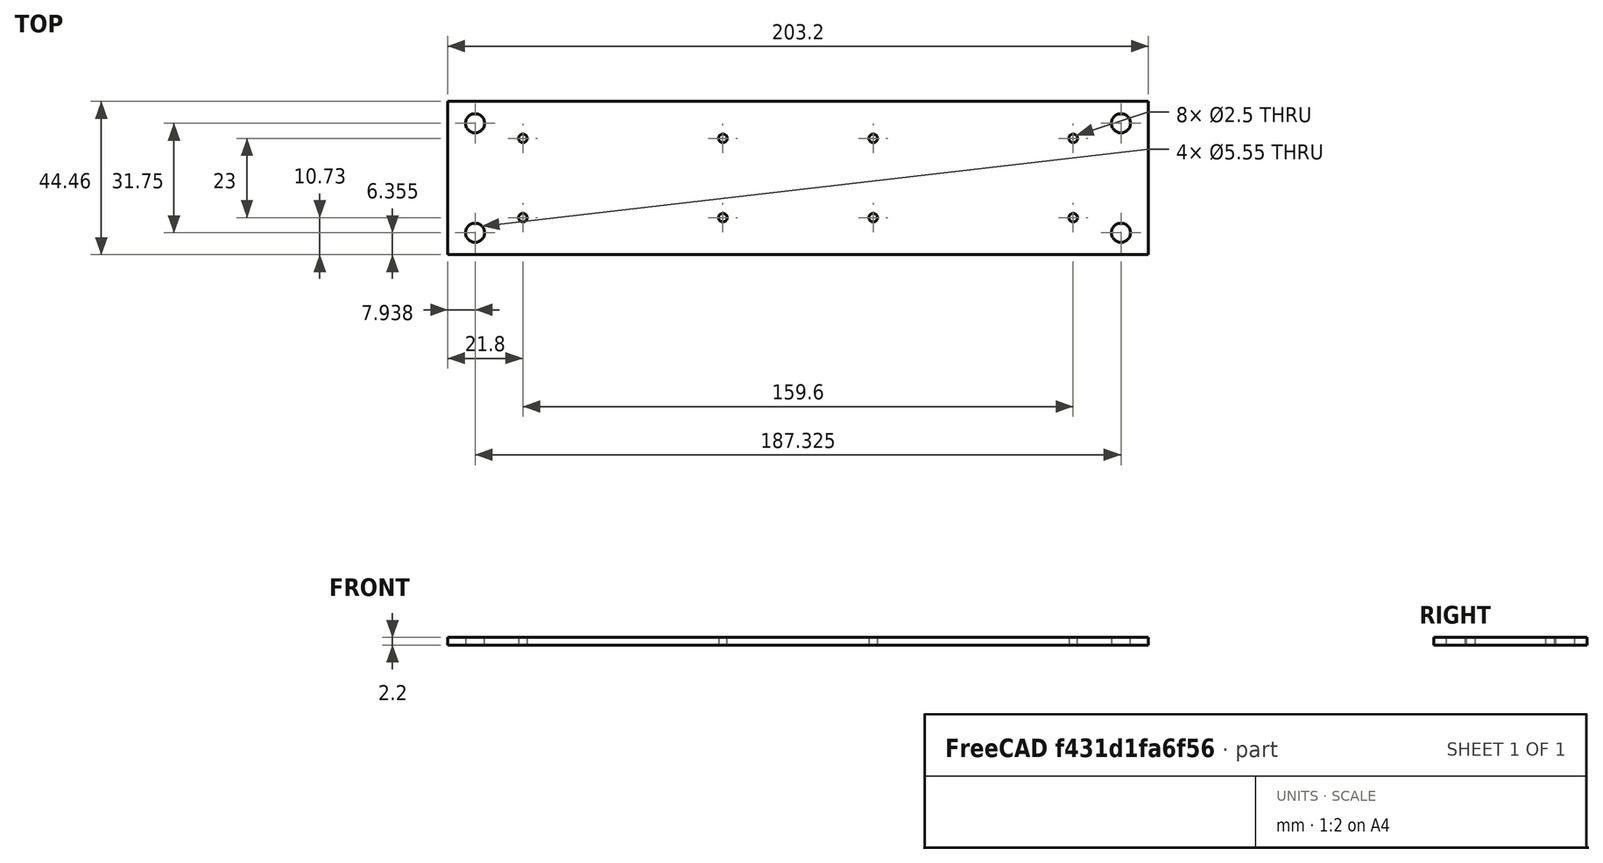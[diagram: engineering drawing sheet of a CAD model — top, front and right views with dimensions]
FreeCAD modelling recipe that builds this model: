
FCSTD DOCUMENT  (FreeCAD 0.19R14555 (Git shallow))
Label: 1U_PiZero_v0
License: All rights reserved
LicenseURL: http://en.wikipedia.org/wiki/All_rights_reserved
objects: PartDesign::Body×2, Sketcher::SketchObject×1, PartDesign::Pad×1
note: 5 computed .brp shape members not serialized (recipe doc carries the construction recipe); baked Part::Feature solids carry a one-line shape summary decoded from their .brp

FEATURE [PartDesign::Body] Body
  Origin = -> Origin
FEATURE [Sketcher::SketchObject] Sketch
  FullyConstrained = false
  MapMode = 5
  Support = -> [XY_Plane001]
  sketch-geometry (16):
    g0: LineSegment StartX=-101.6 StartY=22.225 StartZ=0 EndX=101.6 EndY=22.225 EndZ=0
    g1: LineSegment StartX=101.6 StartY=22.225 StartZ=0 EndX=101.6 EndY=-22.225 EndZ=0
    g2: LineSegment StartX=101.6 StartY=-22.225 StartZ=0 EndX=-101.6 EndY=-22.225 EndZ=0
    g3: LineSegment StartX=-101.6 StartY=-22.225 StartZ=0 EndX=-101.6 EndY=22.225 EndZ=0
    g4: Circle CenterX=-93.6625 CenterY=15.875 CenterZ=0 NormalX=0 NormalY=0 NormalZ=1 AngleXU=0 Radius=2.775
    g5: Circle CenterX=-93.6625 CenterY=-15.875 CenterZ=0 NormalX=0 NormalY=0 NormalZ=1 AngleXU=0 Radius=2.775
    g6: Circle CenterX=93.6625 CenterY=15.875 CenterZ=0 NormalX=0 NormalY=0 NormalZ=1 AngleXU=0 Radius=2.775
    g7: Circle CenterX=93.6625 CenterY=-15.875 CenterZ=0 NormalX=0 NormalY=0 NormalZ=1 AngleXU=0 Radius=2.775
    g8: Circle CenterX=-79.8 CenterY=11.5 CenterZ=0 NormalX=0 NormalY=0 NormalZ=1 AngleXU=0 Radius=1.25
    g9: Circle CenterX=-79.8 CenterY=-11.5 CenterZ=0 NormalX=0 NormalY=0 NormalZ=1 AngleXU=0 Radius=1.25
    g10: Circle CenterX=-21.8 CenterY=11.5 CenterZ=0 NormalX=0 NormalY=0 NormalZ=1 AngleXU=0 Radius=1.25
    g11: Circle CenterX=-21.8 CenterY=-11.5 CenterZ=0 NormalX=0 NormalY=0 NormalZ=1 AngleXU=0 Radius=1.25
    g12: Circle CenterX=21.8 CenterY=11.5 CenterZ=0 NormalX=0 NormalY=0 NormalZ=1 AngleXU=0 Radius=1.25
    g13: Circle CenterX=21.8 CenterY=-11.5 CenterZ=0 NormalX=0 NormalY=0 NormalZ=1 AngleXU=0 Radius=1.25
    g14: Circle CenterX=79.8 CenterY=11.5 CenterZ=0 NormalX=0 NormalY=0 NormalZ=1 AngleXU=0 Radius=1.25
    g15: Circle CenterX=79.8 CenterY=-11.5 CenterZ=0 NormalX=0 NormalY=0 NormalZ=1 AngleXU=0 Radius=1.25
  constraints (31):
    c: Coincident(g0,g1)
    c: Coincident(g1,g2)
    c: Coincident(g2,g3)
    c: Coincident(g3,g0)
    c: Horizontal(g0)
    c: Horizontal(g2)
    c: Vertical(g1)
    c: Vertical(g3)
    c: DistanceX(g0,g0) = 203.2
    c: DistanceY(g3,g3) = 44.45
    c: Symmetric(g0,g2,g-1)
    c: Diameter(g4) = 5.55
    c: DistanceX(g0,g4) = 7.9375
    c: DistanceY(g4,g0) = 6.35
    c: Diameter(g5) = 5.55
    c: Symmetric(g4,g5,g-1)
    c: Diameter(g6) = 5.55
    c: Diameter(g7) = 5.55
    c: Symmetric(g6,g4,g-2)
    c: Symmetric(g7,g5,g-2)
    c: DistanceX(g-1,g12) = 21.8
    c: DistanceY(g2,g9) = 10.725
    c: DistanceY(g1,g15) = 10.725
    c: Diameter(g8) = 2.5
    c: Diameter(g9) = 2.5
    c: Diameter(g10) = 2.5
    c: Diameter(g11) = 2.5
    c: Diameter(g12) = 2.5
    c: Diameter(g13) = 2.5
    c: Diameter(g14) = 2.5
    c: Diameter(g15) = 2.5
FEATURE [PartDesign::Pad] Pad
  Direction = (1,1,1)
  Length = 2.2
  Length2 = 100
  Profile = -> Sketch
  Type = 0
FEATURE [PartDesign::Body] Body001
  Group = -> [Sketch,Pad]
  Origin = -> Origin001
  Tip = -> Pad
